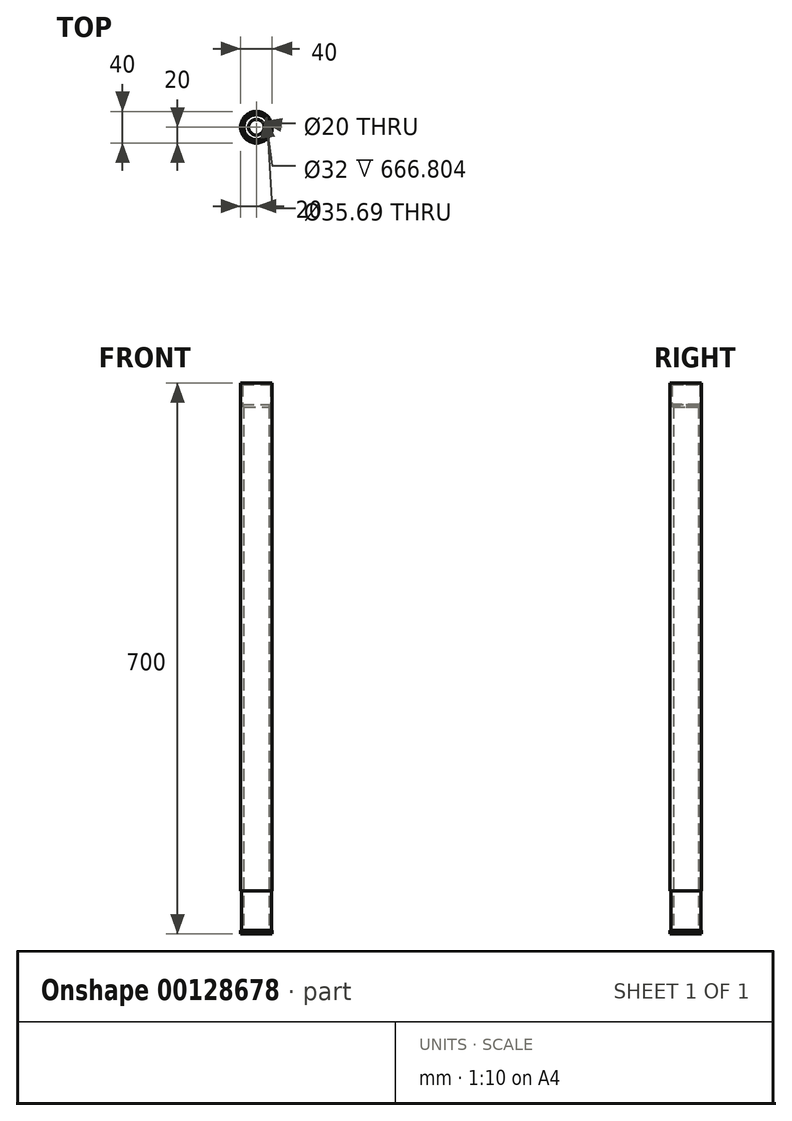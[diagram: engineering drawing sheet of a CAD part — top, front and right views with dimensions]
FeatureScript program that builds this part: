
annotation { "Feature Type Name" : "Feature", "Feature Type Description" : "" }
export const myFeature = defineFeature(function(context is Context, id is Id, definition is map)
    precondition{}
    {
        {
            var Q0;
            Q0=qCreatedBy(makeId("Front.planeOp"),FACE);
            var sketch = newSketch(context, id + "F0", { "sketchPlane" : qUnion([Q0])});
            skLineSegment(sketch, "E0", {"start": v(0, 0) * mm, "end": v(0, 519.9) * mm, "construction": true});
            skLineSegment(sketch, "E1", {"start": v(0, 0) * mm, "end": v(-20, 0) * mm});
            skLineSegment(sketch, "E2", {"start": v(-20, 0) * mm, "end": v(-20, 5) * mm});
            skLineSegment(sketch, "E3", {"start": v(-20, 5) * mm, "end": v(-19, 5) * mm});
            skLineSegment(sketch, "E4", {"start": v(-19, 5) * mm, "end": v(-19, 55) * mm});
            skLineSegment(sketch, "E5", {"start": v(-19, 55) * mm, "end": v(-20, 55) * mm});
            skLineSegment(sketch, "E6", {"start": v(-20, 55) * mm, "end": v(-20, 700) * mm});
            skLineSegment(sketch, "E7", {"start": v(-20, 700) * mm, "end": v(-19, 700) * mm});
            skLineSegment(sketch, "E8", {"start": v(-19, 700) * mm, "end": v(-17.85, 698) * mm});
            skLineSegment(sketch, "E9", {"start": v(-17.85, 698) * mm, "end": v(-17.85, 673) * mm});
            skLineSegment(sketch, "E10", {"start": v(-17.85, 673) * mm, "end": v(-16, 669.8) * mm});
            skLineSegment(sketch, "E11", {"start": v(-16, 669.8) * mm, "end": v(-16, 3) * mm});
            skLineSegment(sketch, "E12", {"start": v(-16, 3) * mm, "end": v(-10, 3) * mm});
            skLineSegment(sketch, "E13", {"start": v(-10, 3) * mm, "end": v(-10, 0) * mm});
            skSolve(sketch);
        }
        {
            var Q0;
            {var subQ0=sQuery(id+"F0.wireOp",EDGE,"E2");Q0=makeQuery(id+"F0.imprint","IMPRINT",FACE,{"disambiguationData":[TD([[makeQuery(id+"F0.imprint","IMPRINT",EDGE,{"derivedFrom":subQ0}),-1.0]])]});}
            var Q1;
            Q1=sQuery(id+"F0.wireOp",EDGE,"E0");
            revolve(context, id + "F1", {"entities" : qUnion([Q0]), "axis" : qUnion([Q1]), "revolveType" : RevolveType.FULL});
        }
    });
